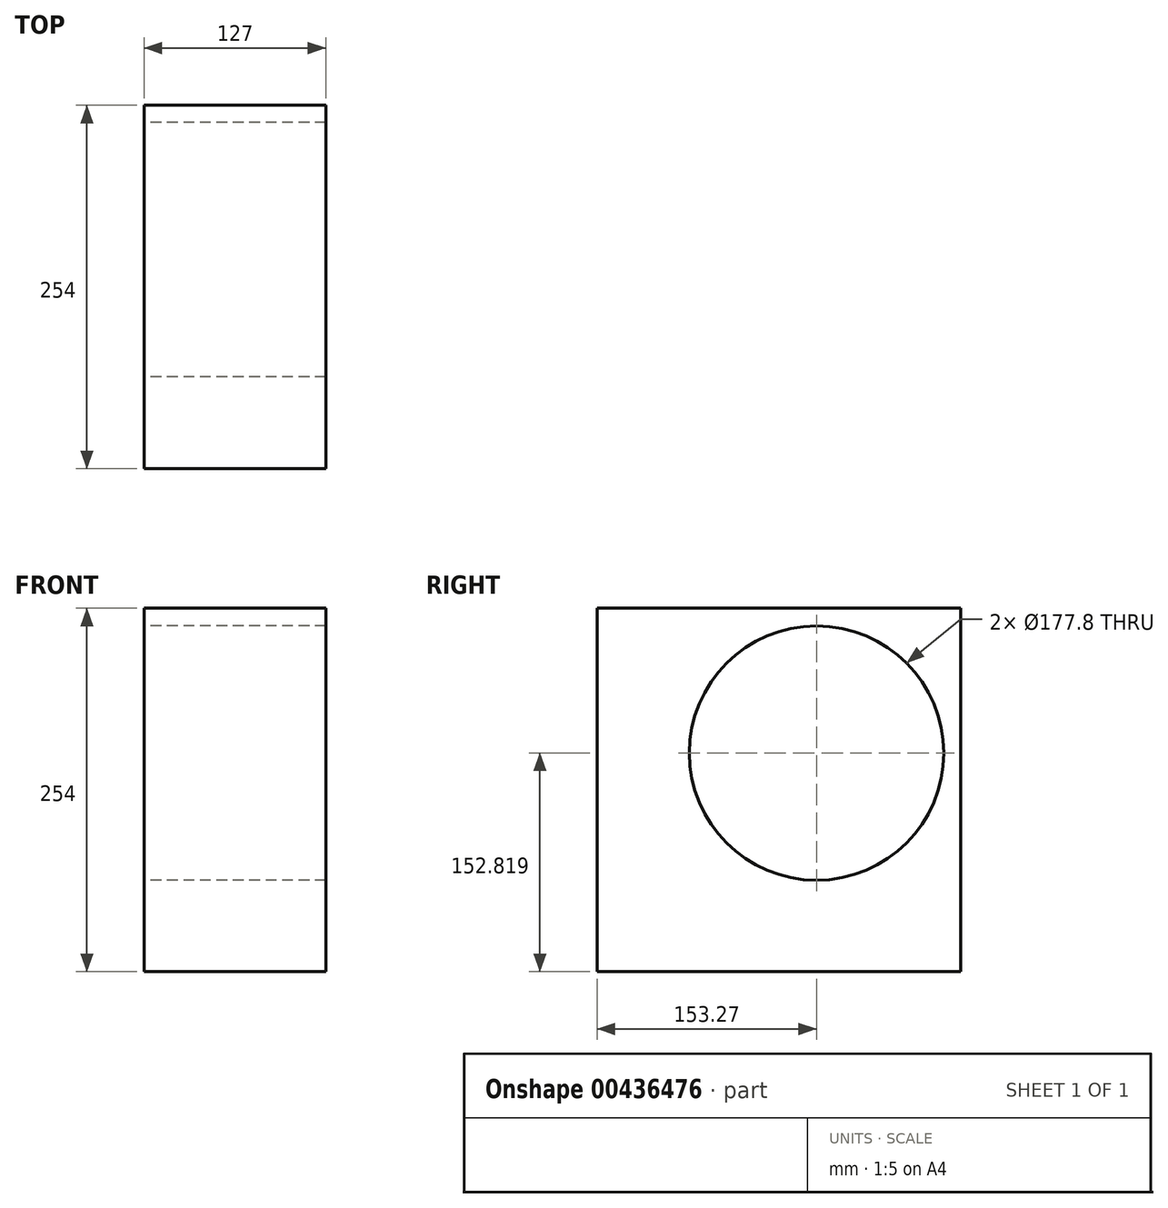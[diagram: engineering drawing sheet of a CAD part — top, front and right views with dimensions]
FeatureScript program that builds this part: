
annotation { "Feature Type Name" : "Feature", "Feature Type Description" : "" }
export const myFeature = defineFeature(function(context is Context, id is Id, definition is map)
    precondition{}
    {
        {
            var Q0;
            Q0=qCreatedBy(makeId("Top.planeOp"),FACE);
            var sketch = newSketch(context, id + "F0", { "sketchPlane" : qUnion([Q0])});
            skLineSegment(sketch, "E0", {"start": v(0, 0) * mm, "end": v(0, 254) * mm});
            skLineSegment(sketch, "E1", {"start": v(0, 254) * mm, "end": v(127, 254) * mm});
            skLineSegment(sketch, "E2", {"start": v(127, 254) * mm, "end": v(127, 0) * mm});
            skLineSegment(sketch, "E3", {"start": v(127, 0) * mm, "end": v(0, 0) * mm});
            skSolve(sketch);
        }
        {
            var Q0;
            Q0=makeQuery(id+"F0.imprint","IMPRINT",FACE,{"disambiguationData":[TD([[makeQuery(id+"F0.imprint","IMPRINT",EDGE,{"derivedFrom":sQuery(id+"F0.wireOp",EDGE,"E0")}),-1.0]])]});
            extrude(context, id + "F1", {"entities" : qUnion([Q0]), "depth" : 254 * mm});
        }
        {
            var Q0;
            Q0=makeQuery(id+"F1.opExtrude","SWEPT_FACE",FACE,{"disambiguationData":[OSD([sQuery(id+"F0.wireOp",EDGE,"E0")])]});
            var sketch = newSketch(context, id + "F2", { "sketchPlane" : qUnion([Q0])});
            skCircle(sketch, "E4", {"center": v(-153.27, 152.82) * mm, "radius": 82.55 * mm});
            skSolve(sketch);
        }
        {
            var Q0;
            Q0=sQuery(id+"F2.wireOp",VERTEX,"E4.center");
            var Q1;
            Q1=makeQuery(id+"F1.opExtrude","SWEPT_BODY",BODY,{"disambiguationData":[OSD([sQuery(id+"F0.wireOp",EDGE,"E0"),sQuery(id+"F0.wireOp",EDGE,"E1"),sQuery(id+"F0.wireOp",EDGE,"E2"),sQuery(id+"F0.wireOp",EDGE,"E3")])]});
            hole(context, id + "F3", {"style" : HoleStyle.C_BORE, "endStyle" : HoleEndStyle.THROUGH, "holeDiameter" : 127 * mm, "cBoreDiameter" : 177.8 * mm, "cBoreDepth" : 127 * mm, "isTappedThrough" : true, "tappedDepth" : 12.7 * mm, "tapClearance" : 3, "locations" : qUnion([Q0]), "scope" : qUnion([Q1])});
        }
    });
